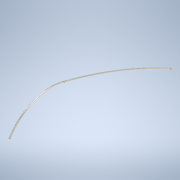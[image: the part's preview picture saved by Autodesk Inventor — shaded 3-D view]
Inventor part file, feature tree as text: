
AUTODESK INVENTOR PART (.ipt)
format: ipt  version: 2022 (Build 260153000, 153)  size: 123,392 bytes
history: native  units: in
note: dims shown in document units (in); Inventor stores cm internally (conversion verified against a paired STEP export)
features: sketch x2, sweep x1
ambient origin geometry x8: Origin, YZ Plane, XZ Plane, XY Plane, X Axis, Y Axis, Z Axis, Center Point
bodies: Solid1 (feature_tree)
feature tree (3):
  sweep  "Sweep1"
  sketch  "Sketch3"  dims[d10=0.001in d11=0.0059in]
  sketch  "Sketch4"  dims[d12=0.013in d13=0.0976in d14=90.0deg d15=0.0in d16=0.0in]
